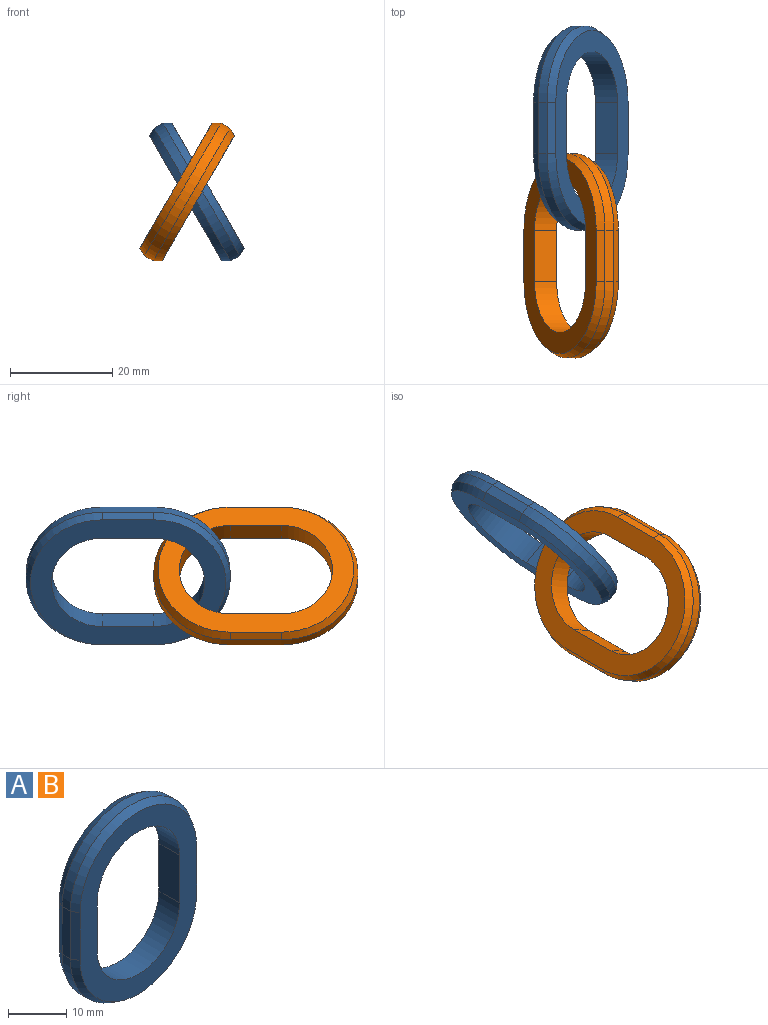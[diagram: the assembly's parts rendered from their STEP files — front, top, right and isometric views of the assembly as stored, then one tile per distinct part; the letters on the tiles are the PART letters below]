
ASSEMBLY  parts=2 mates=1
PART A: 18 faces, bbox 30x5x40 mm
  f0: plane 10x1.5mm, normal (-0.87,0.5,0), area 17.3mm2, adj f1,f4,f12,f17
  f1: plane 10x2mm, normal (-1,0,0), area 20mm2, adj f0,f2,f5,f13
  f2: plane 10x1.5mm, normal (-0.87,-0.5,0), area 17.3mm2, adj f1,f6,f14,f15
  f3: plane 10x5mm, normal (1,0,0), area 50mm2, adj f7,f15,f16,f17
  f4: cone r=15mm half-angle=30deg, axis (0,-1,0), area 79.3mm2, adj f0,f5,f8,f17
  f5: cylinder r=15mm len=30mm, axis (0,-1,0), area 94.2mm2, adj f1,f4,f6,f9
  f6: cone r=14.13mm half-angle=30deg, axis (0,1,0), area 79.3mm2, adj f2,f5,f10,f15
  f7: cylinder r=10mm len=20mm, axis (0,-1,0), area 157.1mm2, adj f3,f11,f15,f17
  f8: plane 10x1.5mm, normal (0.87,0.5,0), area 17.3mm2, adj f4,f9,f12,f17
  f9: plane 10x2mm, normal (1,0,0), area 20mm2, adj f5,f8,f10,f13
  f10: plane 10x1.5mm, normal (0.87,-0.5,0), area 17.3mm2, adj f6,f9,f14,f15
  f11: plane 10x5mm, normal (-1,0,0), area 50mm2, adj f7,f15,f16,f17
  f12: cone r=15mm half-angle=30deg, axis (0,-1,0), area 79.3mm2, adj f0,f8,f13,f17
  f13: cylinder r=15mm len=30mm, axis (0,-1,0), area 94.2mm2, adj f1,f9,f12,f14
  f14: cone r=14.13mm half-angle=30deg, axis (0,1,0), area 79.3mm2, adj f2,f10,f13,f15
  f15: plane 38.27x28.27mm, normal (0,-1,0), area 396.1mm2, adj f2,f3,f6,f7,f10,f11,f14,f16
  f16: cylinder r=10mm len=20mm, axis (0,-1,0), area 157.1mm2, adj f3,f11,f15,f17
  f17: plane 38.27x28.27mm, normal (0,1,0), area 396.1mm2, adj f0,f3,f4,f7,f8,f11,f12,f16
PART B: same geometry as A
PLACE A rot(axis=(0.38,-0.65,0.65),138.6deg) t=(7.68,40,13.49)mm
PLACE B rot(axis=(0.77,-0.45,0.45),104.5deg) t=(5.77,15,13.49)mm
MATE planar A.f0 <-> B.f2  axis (0,0,-1) through (13.45,25,0)mm
